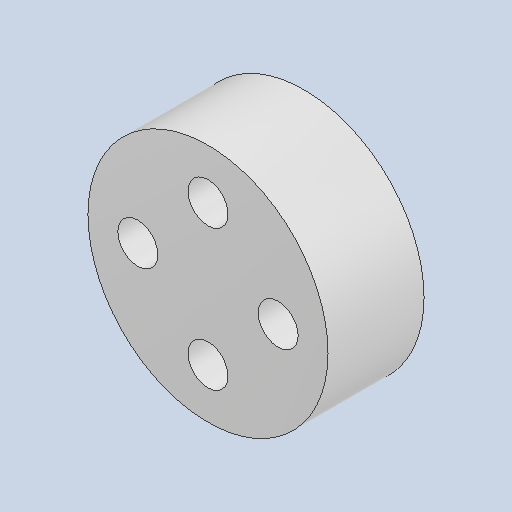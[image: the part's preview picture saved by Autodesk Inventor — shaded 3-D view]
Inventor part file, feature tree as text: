
AUTODESK INVENTOR PART (.ipt)
format: ipt  version: 2023 (Build 270158030, 158C)  size: 124,416 bytes
history: native  units: mm
features: extrude x1, sketch x1
ambient origin geometry x8: Origin, YZ Plane, XZ Plane, XY Plane, X Axis, Y Axis, Z Axis, Center Point
bodies: Solid1 (feature_tree)
feature tree (2):
  extrude  "Extrusion1"  Depth=6.0mm TaperAngle=0.0deg
  sketch  "Sketch1"  dims[d0=15.0mm d1=6.0mm d2=0.0mm]
